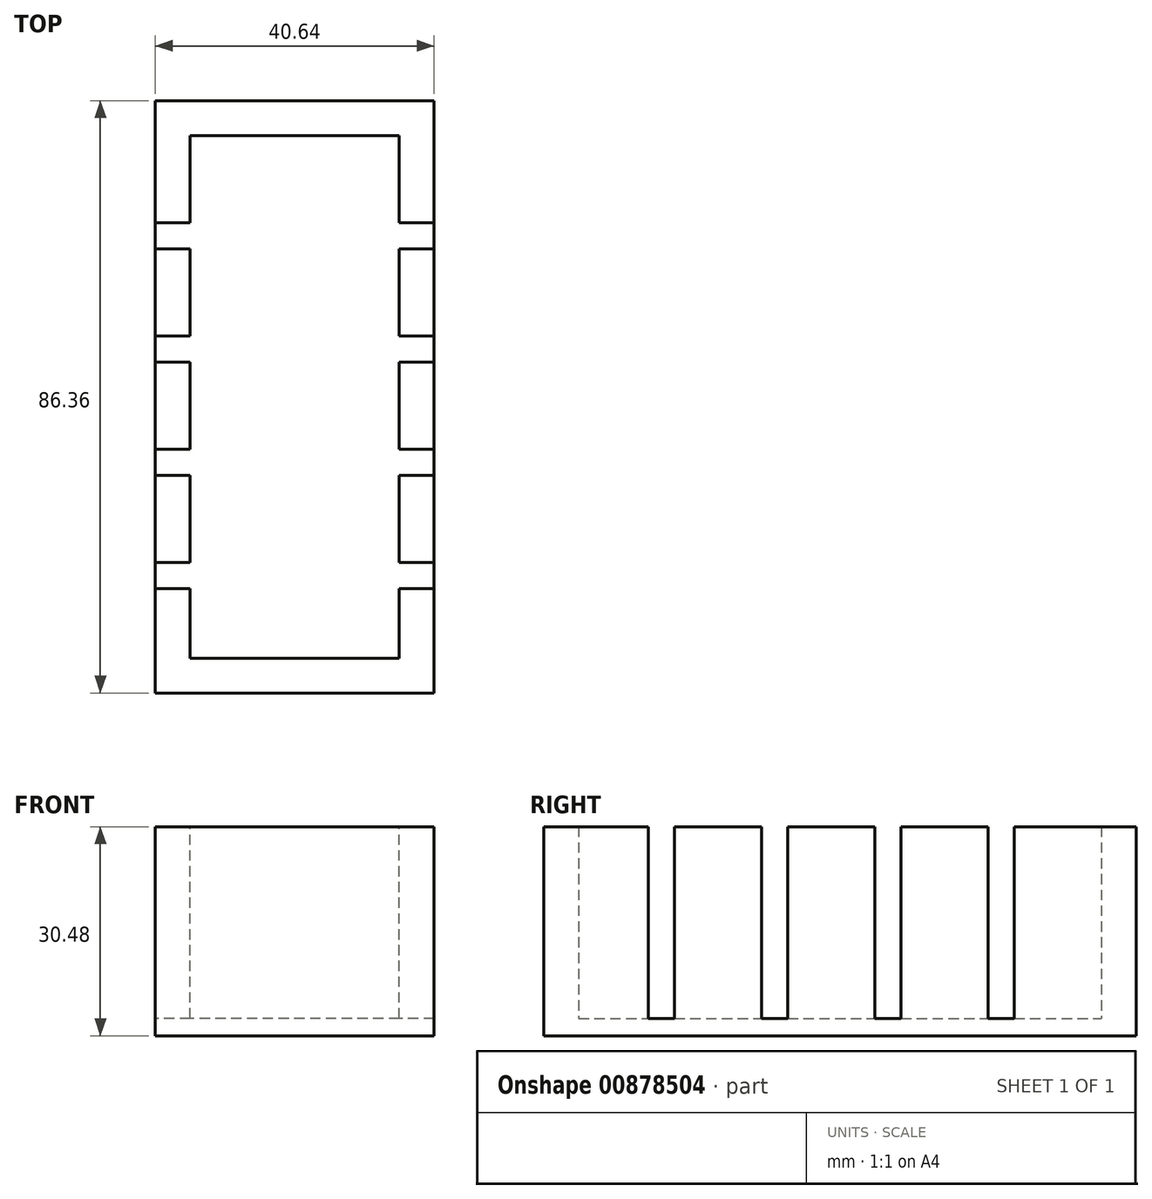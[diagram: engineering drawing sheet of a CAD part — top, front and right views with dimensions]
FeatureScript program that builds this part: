
annotation { "Feature Type Name" : "Feature", "Feature Type Description" : "" }
export const myFeature = defineFeature(function(context is Context, id is Id, definition is map)
    precondition{}
    {
        {
            var Q0;
            Q0=qCreatedBy(makeId("Top.planeOp"),FACE);
            var sketch = newSketch(context, id + "F0", { "sketchPlane" : qUnion([Q0])});
            skLineSegment(sketch, "E0.bottom", {"start": v(15.24, -38.1) * mm, "end": v(-15.24, -38.1) * mm});
            skLineSegment(sketch, "E0.top", {"start": v(15.24, 38.1) * mm, "end": v(-15.24, 38.1) * mm});
            skLineSegment(sketch, "E0.left", {"start": v(15.24, -38.1) * mm, "end": v(15.24, 38.1) * mm});
            skLineSegment(sketch, "E0.right", {"start": v(-15.24, -38.1) * mm, "end": v(-15.24, 38.1) * mm});
            skPoint(sketch, "E0.middle", {"position": v(0, 0) * mm});
            skLineSegment(sketch, "E1.bottom", {"start": v(20.32, -43.18) * mm, "end": v(-20.32, -43.18) * mm});
            skLineSegment(sketch, "E1.top", {"start": v(20.32, 43.18) * mm, "end": v(-20.32, 43.18) * mm});
            skLineSegment(sketch, "E1.left", {"start": v(20.32, -43.18) * mm, "end": v(20.32, 43.18) * mm});
            skLineSegment(sketch, "E1.right", {"start": v(-20.32, -43.18) * mm, "end": v(-20.32, 43.18) * mm});
            skSolve(sketch);
        }
        {
            var Q0;
            Q0=makeQuery(id+"F0.imprint","IMPRINT",FACE,{"disambiguationData":[TD([[makeQuery(id+"F0.imprint","IMPRINT",EDGE,{"derivedFrom":sQuery(id+"F0.wireOp",EDGE,"E0.bottom")}),1.0]])]});
            extrude(context, id + "F1", {"entities" : qUnion([Q0]), "depth" : 30.48 * mm, "offsetDistance" : 25.4 * mm});
        }
        {
            var Q0;
            Q0=makeQuery(id+"F0.imprint","IMPRINT",FACE,{"disambiguationData":[TD([[makeQuery(id+"F0.imprint","IMPRINT",EDGE,{"derivedFrom":sQuery(id+"F0.wireOp",EDGE,"E0.bottom")}),-1.0]])]});
            extrude(context, id + "F2", {"entities" : qUnion([Q0]), "operationType" : NewBodyOperationType.ADD, "depth" : 2.54 * mm, "offsetDistance" : 25.4 * mm});
        }
        {
            var Q0;
            Q0=makeQuery(id+"F1.opExtrude","CAP_FACE",FACE,{"disambiguationData":[OSD([sQuery(id+"F0.wireOp",EDGE,"E0.bottom"),sQuery(id+"F0.wireOp",EDGE,"E0.top"),sQuery(id+"F0.wireOp",EDGE,"E0.left"),sQuery(id+"F0.wireOp",EDGE,"E0.right"),sQuery(id+"F0.wireOp",EDGE,"E1.bottom"),sQuery(id+"F0.wireOp",EDGE,"E1.top"),sQuery(id+"F0.wireOp",EDGE,"E1.left"),sQuery(id+"F0.wireOp",EDGE,"E1.right")])],"isStart":false});
            var sketch = newSketch(context, id + "F3", { "sketchPlane" : qUnion([Q0])});
            skLineSegment(sketch, "E2.bottom", {"start": v(51.73, 21.6) * mm, "end": v(-51.73, 21.59) * mm});
            skLineSegment(sketch, "E2.top", {"start": v(51.73, 25.4) * mm, "end": v(-51.73, 25.4) * mm});
            skLineSegment(sketch, "E2.left", {"start": v(51.73, 21.6) * mm, "end": v(51.73, 25.4) * mm});
            skLineSegment(sketch, "E2.right", {"start": v(-51.73, 21.59) * mm, "end": v(-51.73, 25.4) * mm});
            skPoint(sketch, "E2.middle", {"position": v(0, 23.5) * mm});
            skLineSegment(sketch, "E3.bottom", {"start": v(55.53, 5.08) * mm, "end": v(-55.53, 5.08) * mm});
            skLineSegment(sketch, "E3.top", {"start": v(55.53, 8.9) * mm, "end": v(-55.53, 8.89) * mm});
            skLineSegment(sketch, "E3.left", {"start": v(55.53, 5.08) * mm, "end": v(55.53, 8.9) * mm});
            skLineSegment(sketch, "E3.right", {"start": v(-55.53, 5.08) * mm, "end": v(-55.53, 8.89) * mm});
            skPoint(sketch, "E3.middle", {"position": v(0, 6.98) * mm});
            skLineSegment(sketch, "E4.bottom", {"start": v(45.69, -11.43) * mm, "end": v(-45.69, -11.43) * mm});
            skLineSegment(sketch, "E4.top", {"start": v(45.69, -7.62) * mm, "end": v(-45.69, -7.62) * mm});
            skLineSegment(sketch, "E4.left", {"start": v(45.69, -11.43) * mm, "end": v(45.69, -7.62) * mm});
            skLineSegment(sketch, "E4.right", {"start": v(-45.69, -11.43) * mm, "end": v(-45.69, -7.62) * mm});
            skPoint(sketch, "E4.middle", {"position": v(0, -9.52) * mm});
            skLineSegment(sketch, "E5.bottom", {"start": v(35.85, -27.94) * mm, "end": v(-35.85, -27.94) * mm});
            skLineSegment(sketch, "E5.top", {"start": v(35.85, -24.13) * mm, "end": v(-35.85, -24.13) * mm});
            skLineSegment(sketch, "E5.left", {"start": v(35.85, -27.94) * mm, "end": v(35.85, -24.13) * mm});
            skLineSegment(sketch, "E5.right", {"start": v(-35.85, -27.94) * mm, "end": v(-35.85, -24.13) * mm});
            skPoint(sketch, "E5.middle", {"position": v(0, -26.04) * mm});
            skLineSegment(sketch, "E6.bottom", {"start": v(37.72, -44.45) * mm, "end": v(-37.72, -44.45) * mm});
            skLineSegment(sketch, "E6.top", {"start": v(37.72, -40.64) * mm, "end": v(-37.72, -40.64) * mm});
            skLineSegment(sketch, "E6.left", {"start": v(37.72, -44.45) * mm, "end": v(37.72, -40.64) * mm});
            skLineSegment(sketch, "E6.right", {"start": v(-37.72, -44.45) * mm, "end": v(-37.72, -40.64) * mm});
            skPoint(sketch, "E6.middle", {"position": v(0, -42.55) * mm});
            skPoint(sketch, "E6.middle.positionSnap0", {"position": v(0, -7.62) * mm});
            skPoint(sketch, "E6.centerSnap0", {"position": v(0, -7.62) * mm});
            skLineSegment(sketch, "E7.bottom", {"start": v(44.75, -60.96) * mm, "end": v(-44.75, -60.96) * mm});
            skLineSegment(sketch, "E7.top", {"start": v(44.75, -57.15) * mm, "end": v(-44.75, -57.15) * mm});
            skLineSegment(sketch, "E7.left", {"start": v(44.75, -60.96) * mm, "end": v(44.75, -57.15) * mm});
            skLineSegment(sketch, "E7.right", {"start": v(-44.75, -60.96) * mm, "end": v(-44.75, -57.15) * mm});
            skPoint(sketch, "E7.middle", {"position": v(0, -59.06) * mm});
            skLineSegment(sketch, "E8.bottom", {"start": v(37.25, -77.47) * mm, "end": v(-37.25, -77.47) * mm});
            skLineSegment(sketch, "E8.top", {"start": v(37.25, -73.66) * mm, "end": v(-37.25, -73.66) * mm});
            skLineSegment(sketch, "E8.left", {"start": v(37.25, -77.47) * mm, "end": v(37.25, -73.66) * mm});
            skLineSegment(sketch, "E8.right", {"start": v(-37.25, -77.47) * mm, "end": v(-37.25, -73.66) * mm});
            skPoint(sketch, "E8.middle", {"position": v(0, -75.57) * mm});
            skPoint(sketch, "E9.middle", {"position": v(0, -53.72) * mm});
            skSolve(sketch);
        }
        {
            var Q0;
            {var subQ0=sQuery(id+"F3.wireOp",EDGE,"E2.bottom");var subQ1=makeQuery(id+"F1.opExtrude","CAP_EDGE",EDGE,{"disambiguationData":[OSD([sQuery(id+"F0.wireOp",EDGE,"E1.right")])],"isStart":false});var subQ2=makeQuery(id+"F3.imprint","INTERSECT",VERTEX,{"derivedFrom":[subQ1,subQ0]});Q0=makeQuery(id+"F3.imprint","IMPRINT",FACE,{"disambiguationData":[TD([[makeQuery(id+"F3.imprint","IMPRINT",EDGE,{"disambiguationData":[TD([[subQ2,1.0]])],"derivedFrom":subQ0}),-1.0]])]});}
            var Q1;
            {var subQ0=sQuery(id+"F3.wireOp",EDGE,"E2.bottom");var subQ1=makeQuery(id+"F1.opExtrude","CAP_EDGE",EDGE,{"disambiguationData":[OSD([sQuery(id+"F0.wireOp",EDGE,"E1.left")])],"isStart":false});var subQ2=makeQuery(id+"F3.imprint","INTERSECT",VERTEX,{"derivedFrom":[subQ1,subQ0]});Q1=makeQuery(id+"F3.imprint","IMPRINT",FACE,{"disambiguationData":[TD([[makeQuery(id+"F3.imprint","IMPRINT",EDGE,{"disambiguationData":[TD([[subQ2,-1.0]])],"derivedFrom":subQ0}),-1.0]])]});}
            var Q2;
            {var subQ0=sQuery(id+"F3.wireOp",EDGE,"E3.bottom");var subQ1=makeQuery(id+"F1.opExtrude","CAP_EDGE",EDGE,{"disambiguationData":[OSD([sQuery(id+"F0.wireOp",EDGE,"E1.left")])],"isStart":false});var subQ2=makeQuery(id+"F3.imprint","INTERSECT",VERTEX,{"derivedFrom":[subQ1,subQ0]});Q2=makeQuery(id+"F3.imprint","IMPRINT",FACE,{"disambiguationData":[TD([[makeQuery(id+"F3.imprint","IMPRINT",EDGE,{"disambiguationData":[TD([[subQ2,-1.0]])],"derivedFrom":subQ0}),-1.0]])]});}
            var Q3;
            {var subQ0=sQuery(id+"F3.wireOp",EDGE,"E3.bottom");var subQ1=makeQuery(id+"F1.opExtrude","CAP_EDGE",EDGE,{"disambiguationData":[OSD([sQuery(id+"F0.wireOp",EDGE,"E1.right")])],"isStart":false});var subQ2=makeQuery(id+"F3.imprint","INTERSECT",VERTEX,{"derivedFrom":[subQ1,subQ0]});Q3=makeQuery(id+"F3.imprint","IMPRINT",FACE,{"disambiguationData":[TD([[makeQuery(id+"F3.imprint","IMPRINT",EDGE,{"disambiguationData":[TD([[subQ2,1.0]])],"derivedFrom":subQ0}),-1.0]])]});}
            var Q4;
            {var subQ0=sQuery(id+"F3.wireOp",EDGE,"E4.bottom");var subQ1=makeQuery(id+"F1.opExtrude","CAP_EDGE",EDGE,{"disambiguationData":[OSD([sQuery(id+"F0.wireOp",EDGE,"E1.right")])],"isStart":false});var subQ2=makeQuery(id+"F3.imprint","INTERSECT",VERTEX,{"derivedFrom":[subQ1,subQ0]});Q4=makeQuery(id+"F3.imprint","IMPRINT",FACE,{"disambiguationData":[TD([[makeQuery(id+"F3.imprint","IMPRINT",EDGE,{"disambiguationData":[TD([[subQ2,1.0]])],"derivedFrom":subQ0}),-1.0]])]});}
            var Q5;
            {var subQ0=sQuery(id+"F3.wireOp",EDGE,"E4.bottom");var subQ1=makeQuery(id+"F1.opExtrude","CAP_EDGE",EDGE,{"disambiguationData":[OSD([sQuery(id+"F0.wireOp",EDGE,"E1.left")])],"isStart":false});var subQ2=makeQuery(id+"F3.imprint","INTERSECT",VERTEX,{"derivedFrom":[subQ1,subQ0]});Q5=makeQuery(id+"F3.imprint","IMPRINT",FACE,{"disambiguationData":[TD([[makeQuery(id+"F3.imprint","IMPRINT",EDGE,{"disambiguationData":[TD([[subQ2,-1.0]])],"derivedFrom":subQ0}),-1.0]])]});}
            var Q6;
            {var subQ0=sQuery(id+"F3.wireOp",EDGE,"E5.bottom");var subQ1=makeQuery(id+"F1.opExtrude","CAP_EDGE",EDGE,{"disambiguationData":[OSD([sQuery(id+"F0.wireOp",EDGE,"E1.right")])],"isStart":false});var subQ2=makeQuery(id+"F3.imprint","INTERSECT",VERTEX,{"derivedFrom":[subQ1,subQ0]});Q6=makeQuery(id+"F3.imprint","IMPRINT",FACE,{"disambiguationData":[TD([[makeQuery(id+"F3.imprint","IMPRINT",EDGE,{"disambiguationData":[TD([[subQ2,1.0]])],"derivedFrom":subQ0}),-1.0]])]});}
            var Q7;
            {var subQ0=sQuery(id+"F3.wireOp",EDGE,"E5.bottom");var subQ1=makeQuery(id+"F1.opExtrude","CAP_EDGE",EDGE,{"disambiguationData":[OSD([sQuery(id+"F0.wireOp",EDGE,"E1.left")])],"isStart":false});var subQ2=makeQuery(id+"F3.imprint","INTERSECT",VERTEX,{"derivedFrom":[subQ1,subQ0]});Q7=makeQuery(id+"F3.imprint","IMPRINT",FACE,{"disambiguationData":[TD([[makeQuery(id+"F3.imprint","IMPRINT",EDGE,{"disambiguationData":[TD([[subQ2,-1.0]])],"derivedFrom":subQ0}),-1.0]])]});}
            var Q8;
            {var subQ0=sQuery(id+"F3.wireOp",EDGE,"E6.bottom");var subQ1=makeQuery(id+"F1.opExtrude","CAP_EDGE",EDGE,{"disambiguationData":[OSD([sQuery(id+"F0.wireOp",EDGE,"E1.right")])],"isStart":false});var subQ2=makeQuery(id+"F3.imprint","INTERSECT",VERTEX,{"derivedFrom":[subQ1,subQ0]});Q8=makeQuery(id+"F3.imprint","IMPRINT",FACE,{"disambiguationData":[TD([[makeQuery(id+"F3.imprint","IMPRINT",EDGE,{"disambiguationData":[TD([[subQ2,1.0]])],"derivedFrom":subQ0}),-1.0]])]});}
            var Q9;
            {var subQ0=sQuery(id+"F3.wireOp",EDGE,"E6.bottom");var subQ1=makeQuery(id+"F1.opExtrude","CAP_EDGE",EDGE,{"disambiguationData":[OSD([sQuery(id+"F0.wireOp",EDGE,"E1.left")])],"isStart":false});var subQ2=makeQuery(id+"F3.imprint","INTERSECT",VERTEX,{"derivedFrom":[subQ1,subQ0]});Q9=makeQuery(id+"F3.imprint","IMPRINT",FACE,{"disambiguationData":[TD([[makeQuery(id+"F3.imprint","IMPRINT",EDGE,{"disambiguationData":[TD([[subQ2,-1.0]])],"derivedFrom":subQ0}),-1.0]])]});}
            var Q10;
            {var subQ0=sQuery(id+"F3.wireOp",EDGE,"E7.bottom");var subQ1=makeQuery(id+"F1.opExtrude","CAP_EDGE",EDGE,{"disambiguationData":[OSD([sQuery(id+"F0.wireOp",EDGE,"E1.right")])],"isStart":false});var subQ2=makeQuery(id+"F3.imprint","INTERSECT",VERTEX,{"derivedFrom":[subQ1,subQ0]});Q10=makeQuery(id+"F3.imprint","IMPRINT",FACE,{"disambiguationData":[TD([[makeQuery(id+"F3.imprint","IMPRINT",EDGE,{"disambiguationData":[TD([[subQ2,1.0]])],"derivedFrom":subQ0}),-1.0]])]});}
            var Q11;
            {var subQ0=sQuery(id+"F3.wireOp",EDGE,"E7.bottom");var subQ1=makeQuery(id+"F1.opExtrude","CAP_EDGE",EDGE,{"disambiguationData":[OSD([sQuery(id+"F0.wireOp",EDGE,"E1.left")])],"isStart":false});var subQ2=makeQuery(id+"F3.imprint","INTERSECT",VERTEX,{"derivedFrom":[subQ1,subQ0]});Q11=makeQuery(id+"F3.imprint","IMPRINT",FACE,{"disambiguationData":[TD([[makeQuery(id+"F3.imprint","IMPRINT",EDGE,{"disambiguationData":[TD([[subQ2,-1.0]])],"derivedFrom":subQ0}),-1.0]])]});}
            var Q12;
            {var subQ0=sQuery(id+"F3.wireOp",EDGE,"E8.bottom");var subQ1=makeQuery(id+"F1.opExtrude","CAP_EDGE",EDGE,{"disambiguationData":[OSD([sQuery(id+"F0.wireOp",EDGE,"E1.right")])],"isStart":false});var subQ2=makeQuery(id+"F3.imprint","INTERSECT",VERTEX,{"derivedFrom":[subQ1,subQ0]});Q12=makeQuery(id+"F3.imprint","IMPRINT",FACE,{"disambiguationData":[TD([[makeQuery(id+"F3.imprint","IMPRINT",EDGE,{"disambiguationData":[TD([[subQ2,1.0]])],"derivedFrom":subQ0}),-1.0]])]});}
            var Q13;
            {var subQ0=sQuery(id+"F3.wireOp",EDGE,"E8.bottom");var subQ1=makeQuery(id+"F1.opExtrude","CAP_EDGE",EDGE,{"disambiguationData":[OSD([sQuery(id+"F0.wireOp",EDGE,"E1.left")])],"isStart":false});var subQ2=makeQuery(id+"F3.imprint","INTERSECT",VERTEX,{"derivedFrom":[subQ1,subQ0]});Q13=makeQuery(id+"F3.imprint","IMPRINT",FACE,{"disambiguationData":[TD([[makeQuery(id+"F3.imprint","IMPRINT",EDGE,{"disambiguationData":[TD([[subQ2,-1.0]])],"derivedFrom":subQ0}),-1.0]])]});}
            extrude(context, id + "F4", {"entities" : qUnion([Q0, Q1, Q2, Q3, Q4, Q5, Q6, Q7, Q8, Q9, Q10, Q11, Q12, Q13]), "operationType" : NewBodyOperationType.REMOVE, "oppositeDirection" : true, "depth" : 27.94 * mm, "offsetDistance" : 25.4 * mm});
        }
    });
